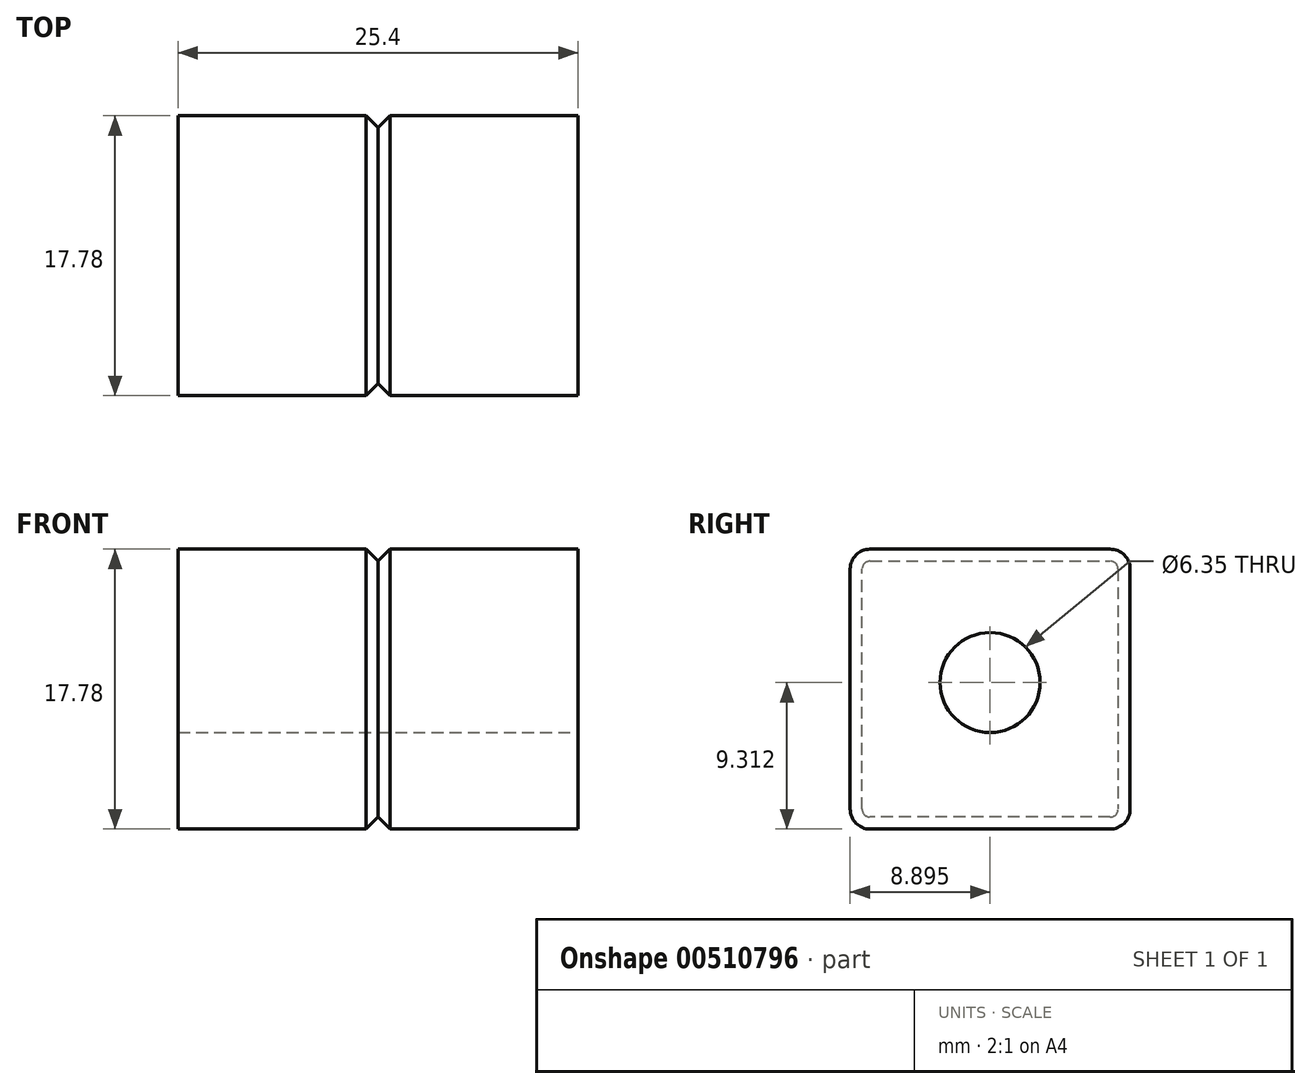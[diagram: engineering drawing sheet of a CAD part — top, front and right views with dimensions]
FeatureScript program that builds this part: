
annotation { "Feature Type Name" : "Feature", "Feature Type Description" : "" }
export const myFeature = defineFeature(function(context is Context, id is Id, definition is map)
    precondition{}
    {
        {
            var Q0;
            Q0=qCreatedBy(makeId("Right.planeOp"),FACE);
            var sketch = newSketch(context, id + "F0", { "sketchPlane" : qUnion([Q0])});
            skLineSegment(sketch, "E0", {"start": v(-46.4, 45.36) * mm, "end": v(-46.4, 30.12) * mm});
            skLineSegment(sketch, "E1", {"start": v(-45.13, 28.85) * mm, "end": v(-29.89, 28.85) * mm});
            skLineSegment(sketch, "E2", {"start": v(-28.62, 30.12) * mm, "end": v(-28.62, 45.36) * mm});
            skLineSegment(sketch, "E3", {"start": v(-29.89, 46.63) * mm, "end": v(-45.13, 46.63) * mm});
            skPoint(sketch, "E4.visualSharp", {"position": v(-46.4, 46.63) * mm});
            skArc(sketch, "E4.filletArc", {"start": v(-45.13, 46.63) * mm, "mid": v(-46.02, 46.26) * mm, "end": v(-46.4, 45.36) * mm});
            skPoint(sketch, "E5.visualSharp", {"position": v(-28.62, 46.63) * mm});
            skArc(sketch, "E5.filletArc", {"start": v(-28.62, 45.36) * mm, "mid": v(-28.99, 46.26) * mm, "end": v(-29.89, 46.63) * mm});
            skPoint(sketch, "E6.visualSharp", {"position": v(-46.4, 28.85) * mm});
            skArc(sketch, "E6.filletArc", {"start": v(-46.4, 30.12) * mm, "mid": v(-46.02, 29.23) * mm, "end": v(-45.13, 28.85) * mm});
            skPoint(sketch, "E7.visualSharp", {"position": v(-28.62, 28.85) * mm});
            skArc(sketch, "E7.filletArc", {"start": v(-29.89, 28.85) * mm, "mid": v(-28.99, 29.23) * mm, "end": v(-28.62, 30.12) * mm});
            skSolve(sketch);
        }
        {
            var Q0;
            Q0=qSketchRegion(id+"F0",true);
            extrude(context, id + "F1", {"entities" : qUnion([Q0]), "depth" : 12.7 * mm, "offsetDistance" : 25.4 * mm});
        }
        {
            var Q0;
            Q0=makeQuery(id+"F1.opExtrude","CAP_EDGE",EDGE,{"disambiguationData":[OSD([sQuery(id+"F0.wireOp",EDGE,"E3")])],"isStart":true});
            var Q1;
            Q1=makeQuery(id+"F1.opExtrude","CAP_EDGE",EDGE,{"disambiguationData":[OSD([sQuery(id+"F0.wireOp",EDGE,"E0")])],"isStart":true});
            chamfer(context, id + "F2", {"entities" : qUnion([Q0, Q1]), "width" : 0.76 * mm, "tangentPropagation" : true});
        }
        {
            var Q0;
            Q0=makeQuery(id+"F1.opExtrude","SWEPT_BODY",BODY,{"disambiguationData":[OSD([sQuery(id+"F0.wireOp",EDGE,"E0"),sQuery(id+"F0.wireOp",EDGE,"E1"),sQuery(id+"F0.wireOp",EDGE,"E2"),sQuery(id+"F0.wireOp",EDGE,"E3"),sQuery(id+"F0.wireOp",EDGE,"E4.filletArc"),sQuery(id+"F0.wireOp",EDGE,"E5.filletArc"),sQuery(id+"F0.wireOp",EDGE,"E6.filletArc"),sQuery(id+"F0.wireOp",EDGE,"E7.filletArc")])]});
            var Q1;
            Q1=qCreatedBy(makeId("Right.planeOp"),FACE);
            mirror(context, id + "F3", {"operationType" : NewBodyOperationType.ADD, "entities" : qUnion([Q0]), "mirrorPlane" : qUnion([Q1])});
        }
        {
            var Q0;
            Q0=makeQuery(id+"F1.opExtrude","CAP_FACE",FACE,{"disambiguationData":[OSD([sQuery(id+"F0.wireOp",EDGE,"E0"),sQuery(id+"F0.wireOp",EDGE,"E1"),sQuery(id+"F0.wireOp",EDGE,"E2"),sQuery(id+"F0.wireOp",EDGE,"E3"),sQuery(id+"F0.wireOp",EDGE,"E4.filletArc"),sQuery(id+"F0.wireOp",EDGE,"E5.filletArc"),sQuery(id+"F0.wireOp",EDGE,"E6.filletArc"),sQuery(id+"F0.wireOp",EDGE,"E7.filletArc")])],"isStart":false});
            var sketch = newSketch(context, id + "F4", { "sketchPlane" : qUnion([Q0])});
            skCircle(sketch, "E8", {"center": v(-37.5, 38.16) * mm, "radius": 3.18 * mm});
            skPoint(sketch, "E8.centerSnap0", {"position": v(-37.5, 46.63) * mm});
            skSolve(sketch);
        }
        {
            var Q0;
            Q0=makeQuery(id+"F4.imprint","IMPRINT",FACE,{"disambiguationData":[TD([[makeQuery(id+"F4.imprint","IMPRINT",EDGE,{"derivedFrom":sQuery(id+"F4.wireOp",EDGE,"E8")}),1.0]])]});
            extrude(context, id + "F5", {"entities" : qUnion([Q0]), "operationType" : NewBodyOperationType.REMOVE, "endBound" : BoundingType.THROUGH_ALL, "oppositeDirection" : true, "depth" : 25.4 * mm, "offsetDistance" : 25.4 * mm});
        }
    });
